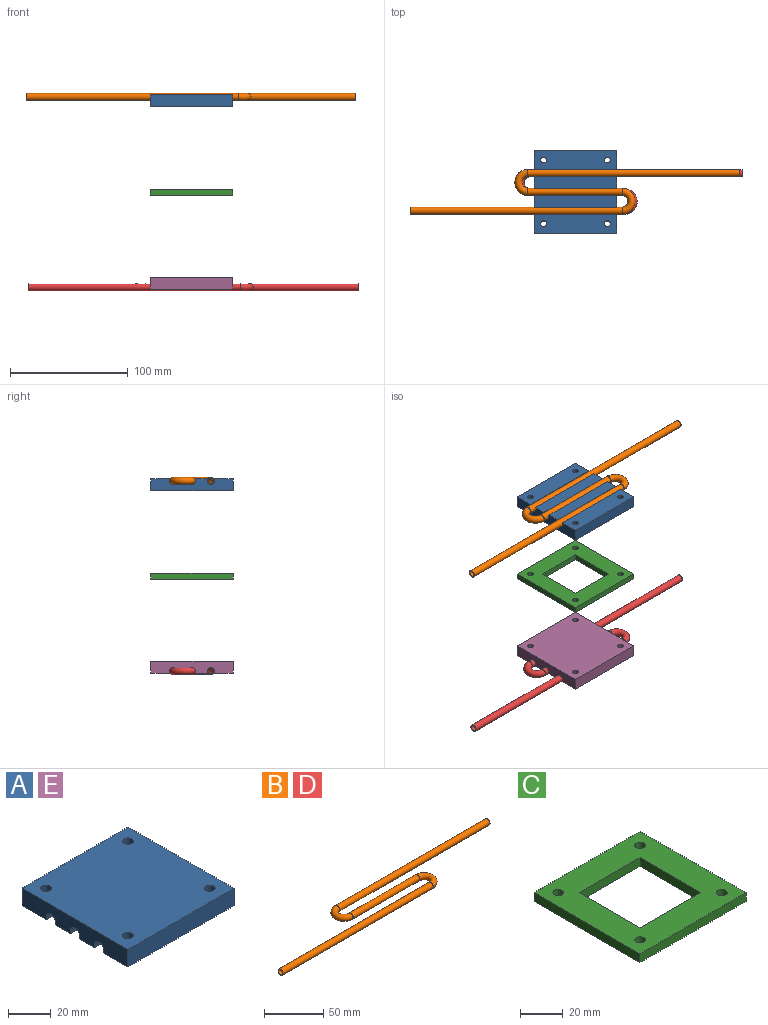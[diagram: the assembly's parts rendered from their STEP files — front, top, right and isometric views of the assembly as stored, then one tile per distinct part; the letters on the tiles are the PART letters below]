
ASSEMBLY  parts=5 mates=4
PART A: 22 faces, bbox 70x70x10 mm
  f0: plane 70x10mm, normal (1,0,0), area 626.1mm2, adj f2,f3,f4,f5,f9,f11,f12,f13
  f1: plane 70x10mm, normal (-1,0,0), area 626.1mm2, adj f2,f3,f4,f5,f9,f11,f12,f13
  f2: plane 70x10mm, normal (0,0,-1), area 700mm2, adj f0,f1,f15,f19
  f3: plane 70x16mm, normal (0,0,-1), area 1080.7mm2, adj f0,f1,f5,f8,f10,f16
  f4: plane 70x10mm, normal (0,0,-1), area 700mm2, adj f0,f1,f13,f18
  f5: plane 70x10mm, normal (0,1,0), area 700mm2, adj f0,f1,f3,f11
  f6: cylinder r=2.5mm len=10mm, axis (0,0,-1), area 157.1mm2, adj f11,f12
  f7: cylinder r=2.5mm len=10mm, axis (0,0,-1), area 157.1mm2, adj f11,f12
  f8: cylinder r=2.5mm len=10mm, axis (0,0,-1), area 157.1mm2, adj f3,f11
  f9: plane 70x10mm, normal (0,-1,0), area 700mm2, adj f0,f1,f11,f12
  f10: cylinder r=2.5mm len=10mm, axis (0,0,-1), area 157.1mm2, adj f3,f11
  f11: plane 70x70mm, normal (0,0,1), area 4821.5mm2, adj f0,f1,f5,f6,f7,f8,f9,f10
  f12: plane 70x16mm, normal (0,0,-1), area 1080.7mm2, adj f0,f1,f6,f7,f9,f21
  f13: plane 70x1.75mm, normal (0,-1,0), area 122.5mm2, adj f0,f1,f4,f14
  f14: cylinder r=3mm len=70mm, axis (1,0,0), area 659.7mm2, adj f0,f1,f13,f15
  f15: plane 70x1.75mm, normal (0,1,0), area 122.5mm2, adj f0,f1,f2,f14
  f16: plane 70x1.75mm, normal (0,-1,0), area 122.5mm2, adj f0,f1,f3,f17
  f17: cylinder r=3mm len=70mm, axis (1,0,0), area 659.7mm2, adj f0,f1,f16,f18
  f18: plane 70x1.75mm, normal (0,1,0), area 122.5mm2, adj f0,f1,f4,f17
  f19: plane 70x1.75mm, normal (0,-1,0), area 122.5mm2, adj f0,f1,f2,f20
  f20: cylinder r=3mm len=70mm, axis (1,0,0), area 659.7mm2, adj f0,f1,f19,f21
  f21: plane 70x1.75mm, normal (0,1,0), area 122.5mm2, adj f0,f1,f12,f20
PART B: 12 faces, bbox 280x39.8x6 mm
  f0: cylinder r=2.5mm len=180mm, axis (-1,0,0), area 2827.4mm2, adj f1,f5
  f1: torus R=8mm, axis (0,0,1), area 394.8mm2, adj f0,f2
  f2: cylinder r=2.5mm len=80mm, axis (1,0,0), area 1256.6mm2, adj f1,f3
  f3: torus R=8mm, axis (0,0,-1), area 394.8mm2, adj f2,f4
  f4: cylinder r=2.5mm len=180mm, axis (-1,0,0), area 2827.4mm2, adj f3,f6
  f5: plane 6x6mm, normal (1,0,0), area 8.6mm2, adj f0,f7
  f6: plane 6x6mm, normal (-1,0,0), area 8.6mm2, adj f4,f11
  f7: cylinder r=3mm len=180mm, axis (-1,0,0), area 3392.9mm2, adj f5,f8
  f8: torus R=8mm, axis (0,0,1), area 473.7mm2, adj f7,f9
  f9: cylinder r=3mm len=80mm, axis (1,0,0), area 1508mm2, adj f8,f10
  f10: torus R=8mm, axis (0,0,-1), area 473.7mm2, adj f9,f11
  f11: cylinder r=3mm len=180mm, axis (-1,0,0), area 3392.9mm2, adj f6,f10
PART C: 14 faces, bbox 70x70x5 mm
  f0: plane 70x70mm, normal (0,0,1), area 3221.5mm2, adj f2,f3,f4,f5,f6,f7,f8,f9
  f1: plane 70x70mm, normal (0,0,-1), area 3221.5mm2, adj f2,f3,f4,f5,f6,f7,f8,f9
  f2: plane 70x5mm, normal (1,0,0), area 350mm2, adj f0,f1,f3,f8
  f3: plane 70x5mm, normal (0,1,0), area 350mm2, adj f0,f1,f2,f4
  f4: plane 70x5mm, normal (-1,0,0), area 350mm2, adj f0,f1,f3,f8
  f5: cylinder r=2.5mm len=5mm, axis (0,0,-1), area 78.5mm2, adj f0,f1
  f6: cylinder r=2.5mm len=5mm, axis (0,0,-1), area 78.5mm2, adj f0,f1
  f7: cylinder r=2.5mm len=5mm, axis (0,0,-1), area 78.5mm2, adj f0,f1
  f8: plane 70x5mm, normal (0,-1,0), area 350mm2, adj f0,f1,f2,f4
  f9: cylinder r=2.5mm len=5mm, axis (0,0,-1), area 78.5mm2, adj f0,f1
  f10: plane 40x5mm, normal (-1,0,0), area 200mm2, adj f0,f1,f11,f13
  f11: plane 40x5mm, normal (0,-1,0), area 200mm2, adj f0,f1,f10,f12
  f12: plane 40x5mm, normal (1,0,0), area 200mm2, adj f0,f1,f11,f13
  f13: plane 40x5mm, normal (0,1,0), area 200mm2, adj f0,f1,f10,f12
PART D: same geometry as B
PART E: same geometry as A
PLACE A rot(axis=(1,0,0),180deg) t=(0,0,10)mm
PLACE B t=(-0.46,0,6.5)mm
PLACE C t=(0,0,-85.17)mm
PLACE D t=(1.35,0,-154.9)mm
PLACE E t=(0,0,-154.9)mm
MATE slider B.f7 <-> A.f20  axis (1,0,0) through (139.54,16,8.25)mm
MATE slider C.f6 <-> A.f8  axis (0,0,1) through (-27,-27,-70.17)mm
MATE slider D.f7 <-> E.f17  axis (1,0,0) through (141.35,16,-153.15)mm
MATE slider A.f11 <-> E.f11  axis (0,0,-1) through (0,0,0)mm
